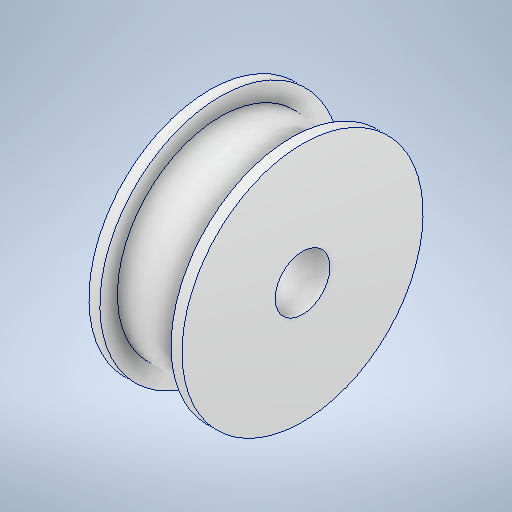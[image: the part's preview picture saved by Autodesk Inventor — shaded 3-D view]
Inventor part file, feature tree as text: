
AUTODESK INVENTOR PART (.ipt)
format: ipt  version: 2025.1 (Build 291241020, 241B)  size: 274,432 bytes
history: native  units: mm
features: revolve x1, mirror x1, sketch x1
ambient origin geometry x8: Origin, YZ Plane, XZ Plane, XY Plane, X Axis, Y Axis, Z Axis, Center Point
bodies: Solid1 (feature_tree)
feature tree (3):
  revolve  "Revolution1"  [1 undecoded]
  mirror  "Mirror2"
  sketch  "Sketch1"  dims[d0=4.25mm d1=3.25mm d2=9.4mm d3=11.0mm d4=2.5mm d5=360.0deg d8=1.0mm]
note: 1 required parameter value undecoded (feature->parameter linkage not recoverable at this tier; creation-order binding heuristic only, values carry confidence <= 0.55)
